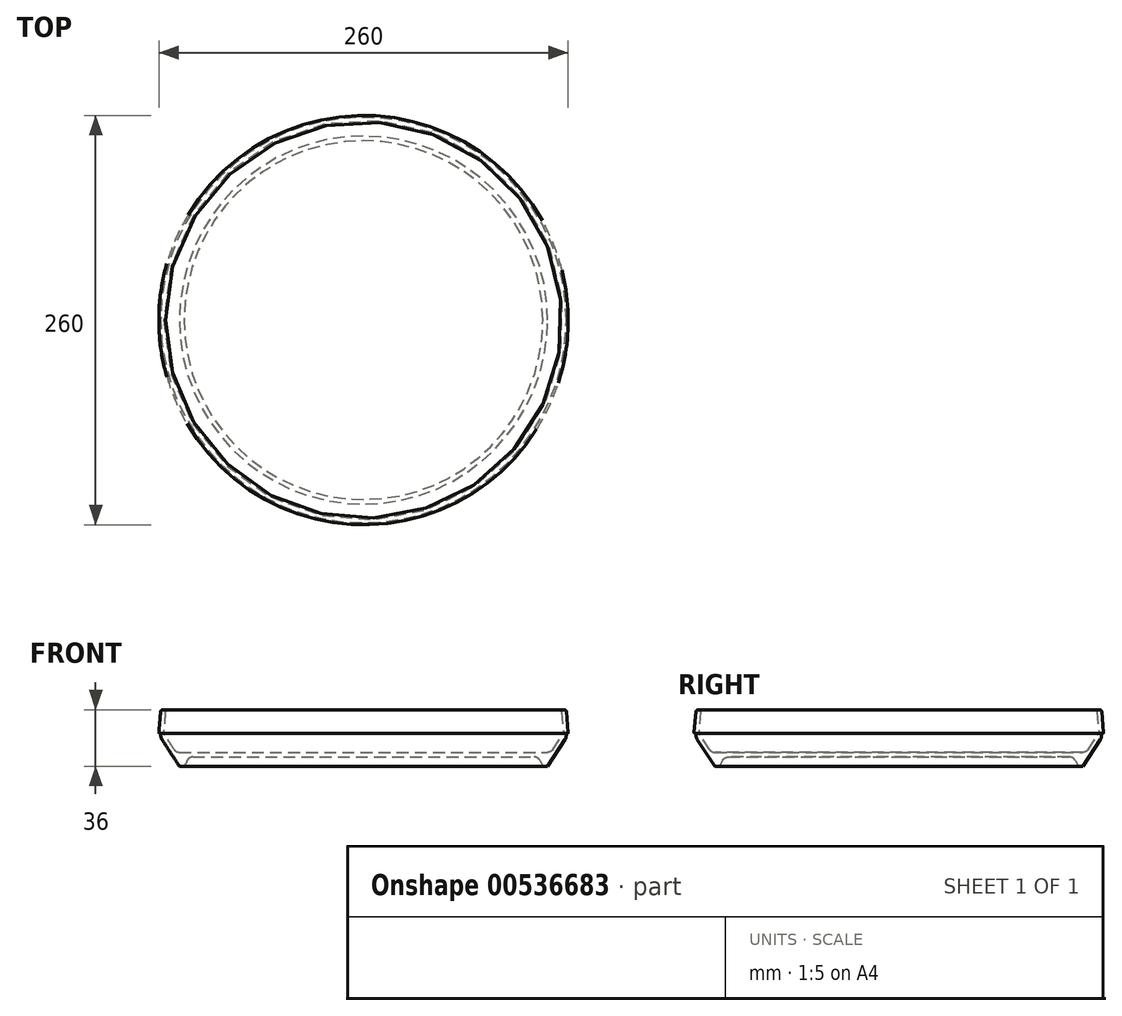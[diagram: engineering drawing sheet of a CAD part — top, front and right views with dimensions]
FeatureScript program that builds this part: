
annotation { "Feature Type Name" : "Feature", "Feature Type Description" : "" }
export const myFeature = defineFeature(function(context is Context, id is Id, definition is map)
    precondition{}
    {
        {
            var Q0;
            Q0=qCreatedBy(makeId("Front.planeOp"),FACE);
            var sketch = newSketch(context, id + "F0", { "sketchPlane" : qUnion([Q0])});
            skLineSegment(sketch, "E0", {"start": v(0, 6) * mm, "end": v(108.32, 6) * mm});
            skLineSegment(sketch, "E1", {"start": v(112.05, 3.7) * mm, "end": v(113.9, 0) * mm});
            skLineSegment(sketch, "E2", {"start": v(113.9, 0) * mm, "end": v(116.9, 0) * mm});
            skLineSegment(sketch, "E3", {"start": v(116.9, 0) * mm, "end": v(128.08, 17.23) * mm});
            skLineSegment(sketch, "E4", {"start": v(130, 21.54) * mm, "end": v(128.84, 34.82) * mm});
            skLineSegment(sketch, "E5", {"start": v(127.43, 36) * mm, "end": v(127.03, 35.97) * mm});
            skLineSegment(sketch, "E6", {"start": v(125.85, 34.56) * mm, "end": v(126.9, 22.54) * mm});
            skLineSegment(sketch, "E7", {"start": v(126.24, 19.9) * mm, "end": v(120.4, 10.9) * mm});
            skLineSegment(sketch, "E8", {"start": v(116.9, 9) * mm, "end": v(0, 9) * mm});
            skLineSegment(sketch, "E9", {"start": v(0, 9) * mm, "end": v(0, 6) * mm});
            skPoint(sketch, "E10.visualSharp", {"position": v(110.9, 6) * mm});
            skArc(sketch, "E10.filletArc", {"start": v(112.05, 3.7) * mm, "mid": v(110.51, 5.38) * mm, "end": v(108.32, 6) * mm});
            skPoint(sketch, "E11.visualSharp", {"position": v(119.16, 9) * mm});
            skArc(sketch, "E11.filletArc", {"start": v(116.9, 9) * mm, "mid": v(118.9, 9.5) * mm, "end": v(120.4, 10.9) * mm});
            skPoint(sketch, "E12.visualSharp", {"position": v(127.03, 21.1) * mm});
            skArc(sketch, "E12.filletArc", {"start": v(126.24, 19.9) * mm, "mid": v(126.8, 21.16) * mm, "end": v(126.9, 22.54) * mm});
            skPoint(sketch, "E13.visualSharp", {"position": v(129.07, 18.74) * mm});
            skArc(sketch, "E13.filletArc", {"start": v(128.08, 17.23) * mm, "mid": v(128.59, 18.31) * mm, "end": v(128.76, 19.5) * mm});
            skPoint(sketch, "E14.visualSharp", {"position": v(128.73, 36.11) * mm});
            skArc(sketch, "E14.filletArc", {"start": v(128.84, 34.82) * mm, "mid": v(128.38, 35.7) * mm, "end": v(127.43, 36) * mm});
            skPoint(sketch, "E15.visualSharp", {"position": v(125.74, 35.85) * mm});
            skArc(sketch, "E15.filletArc", {"start": v(127.03, 35.97) * mm, "mid": v(126.15, 35.5) * mm, "end": v(125.85, 34.56) * mm});
            skLineSegment(sketch, "E16", {"start": v(130, 21.54) * mm, "end": v(130, 36.11) * mm, "construction": true});
            skLineSegment(sketch, "E17", {"start": v(0, 0) * mm, "end": v(0, 34.82) * mm, "construction": true});
            skLineSegment(sketch, "E18", {"start": v(128.76, 19.5) * mm, "end": v(128.76, 20.5) * mm});
            skArc(sketch, "E19", {"start": v(129.5, 21) * mm, "mid": v(129.87, 21.16) * mm, "end": v(130, 21.54) * mm});
            skLineSegment(sketch, "E20", {"start": v(129.5, 21) * mm, "end": v(129.26, 21) * mm});
            skArc(sketch, "E21", {"start": v(129.26, 21) * mm, "mid": v(128.9, 20.85) * mm, "end": v(128.76, 20.5) * mm});
            skSolve(sketch);
        }
        {
            var Q0;
            Q0=qSketchRegion(id+"F0",true);
            var Q1;
            Q1=sQuery(id+"F0.wireOp",EDGE,"E17");
            revolve(context, id + "F1", {"entities" : qUnion([Q0]), "axis" : qUnion([Q1]), "revolveType" : RevolveType.FULL});
        }
    });
